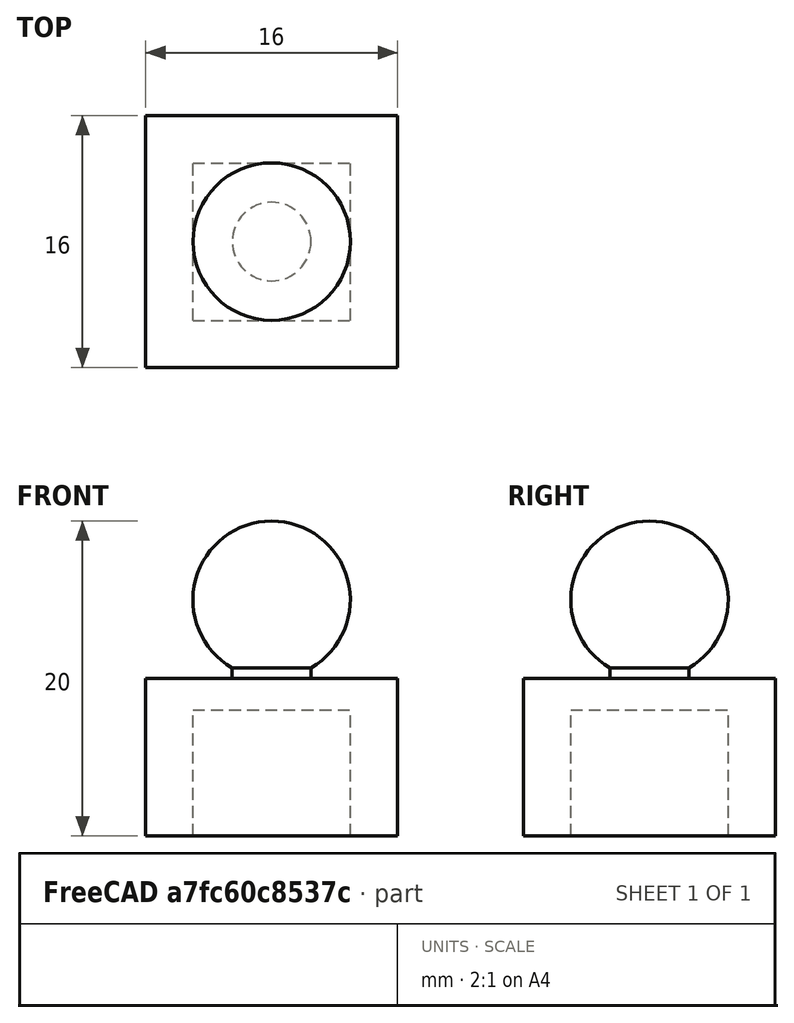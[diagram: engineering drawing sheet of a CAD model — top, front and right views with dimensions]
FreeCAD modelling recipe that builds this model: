
FCSTD DOCUMENT  (FreeCAD 0.18.3R)
Label: sphere2
License: All rights reserved
LicenseURL: http://en.wikipedia.org/wiki/All_rights_reserved
objects: Part::Box×2, Part::Cylinder×1, Part::Sphere×1, Part::MultiFuse×1, Part::Cut×1
note: 6 computed .brp shape members not serialized (recipe doc carries the construction recipe); baked Part::Feature solids carry a one-line shape summary decoded from their .brp

FEATURE [Part::Box] Box  label="Cube"
  AttacherType = Attacher::AttachEngine3D
  Height = 10
  Length = 16
  Placement = pos=(-8,-8,0) rot=(0,0,1;0rad)
  Width = 16
FEATURE [Part::Cylinder] Cylinder
  Angle = 360
  AttacherType = Attacher::AttachEngine3D
  Height = 5
  Placement = pos=(0,0,10) rot=(0,0,1;0rad)
  Radius = 2.5
FEATURE [Part::Sphere] Sphere
  Angle1 = -90
  Angle2 = 90
  Angle3 = 360
  AttacherType = Attacher::AttachEngine3D
  Placement = pos=(0,0,15) rot=(0,0,1;0rad)
  Radius = 5
FEATURE [Part::MultiFuse] Fusion
  Shapes = -> [Box,Cylinder,Sphere]
FEATURE [Part::Box] Box001  label="Cube001"
  AttacherType = Attacher::AttachEngine3D
  Height = 8
  Length = 10
  Placement = pos=(-5,-5,0) rot=(0,0,1;0rad)
  Width = 10
FEATURE [Part::Cut] Cut
  Base = -> Fusion
  Tool = -> Box001
